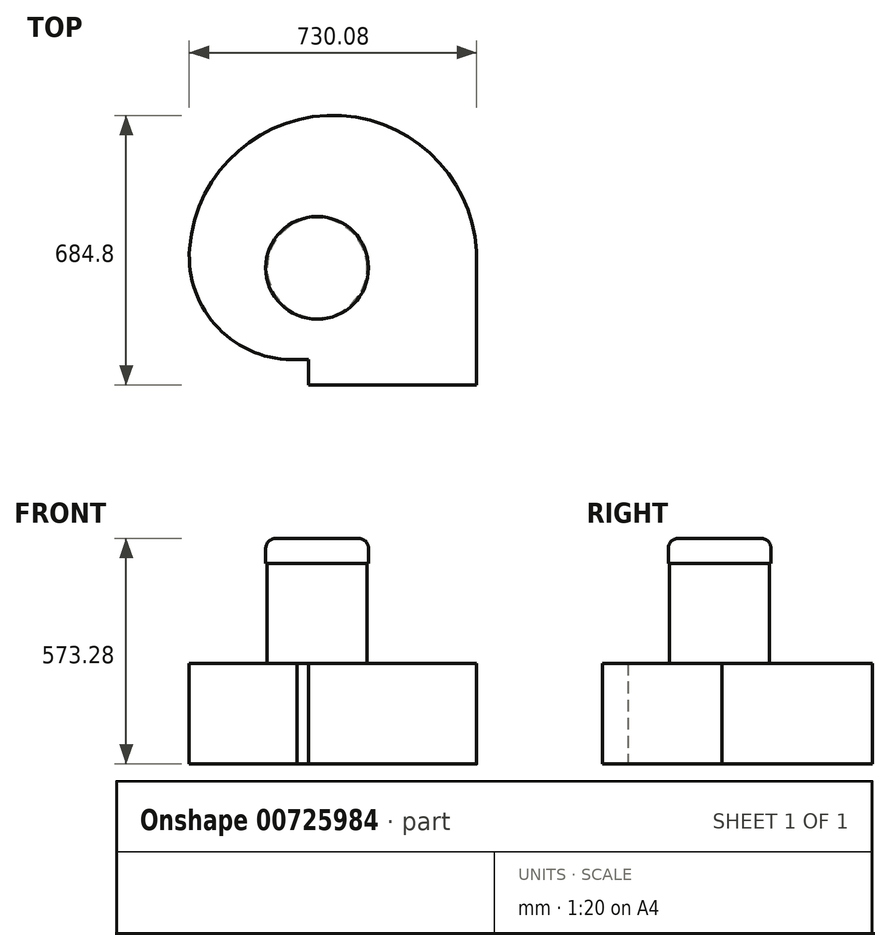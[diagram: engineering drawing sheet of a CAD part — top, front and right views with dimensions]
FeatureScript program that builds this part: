
annotation { "Feature Type Name" : "Feature", "Feature Type Description" : "" }
export const myFeature = defineFeature(function(context is Context, id is Id, definition is map)
    precondition{}
    {
        {
            var Q0;
            Q0=qCreatedBy(makeId("Top.planeOp"),FACE);
            var sketch = newSketch(context, id + "F0", { "sketchPlane" : qUnion([Q0])});
            skLineSegment(sketch, "E0.bottom", {"start": v(0, 0) * mm, "end": v(60.56, 0) * mm, "construction": true});
            skLineSegment(sketch, "E0.top", {"start": v(0, 43.5) * mm, "end": v(60.56, 43.5) * mm, "construction": true});
            skLineSegment(sketch, "E0.left", {"start": v(0, 0) * mm, "end": v(0, 43.5) * mm, "construction": true});
            skLineSegment(sketch, "E0.right", {"start": v(60.56, 0) * mm, "end": v(60.56, 43.5) * mm, "construction": true});
            skLineSegment(sketch, "E1", {"start": v(60.56, 43.5) * mm, "end": v(333.53, 43.5) * mm, "construction": true});
            skLineSegment(sketch, "E2", {"start": v(0, 43.5) * mm, "end": v(0, 380.21) * mm, "construction": true});
            skLineSegment(sketch, "E3", {"start": v(0, 0) * mm, "end": v(-395.45, 0) * mm, "construction": true});
            skLineSegment(sketch, "E4", {"start": v(60.56, 0) * mm, "end": v(60.56, -239.05) * mm, "construction": true});
            skArc(sketch, "E5.MirrorCS", {"start": v(-333.53, 43.5) * mm, "mid": v(52.4, 380.85) * mm, "end": v(395.45, 0) * mm});
            skLineSegment(sketch, "E6.MirrorCS", {"start": v(395.45, 0) * mm, "end": v(395.45, -303.3) * mm});
            skLineSegment(sketch, "E7.MirrorCS", {"start": v(395.45, -303.3) * mm, "end": v(-31.52, -303.3) * mm});
            skLineSegment(sketch, "E8.MirrorCS", {"start": v(-31.52, -239.05) * mm, "end": v(-31.52, -303.3) * mm});
            skLineSegment(sketch, "E9.MirrorCS", {"start": v(-60.56, -239.05) * mm, "end": v(-31.52, -239.05) * mm});
            skArc(sketch, "E10.MirrorCS", {"start": v(-333.53, 43.5) * mm, "mid": v(-260.36, -158.94) * mm, "end": v(-60.56, -239.05) * mm});
            skSolve(sketch);
        }
        {
            var Q0;
            Q0 = qSketchRegion(id + "F0", true);
            extrude(context, id + "F1", {"entities" : qUnion([Q0]), "depth" : 255.52 * mm, "offsetDistance" : 25.4 * mm});
        }
        {
            var Q0;
            Q0=makeQuery(id+"F1.opExtrude","CAP_FACE",FACE,{"disambiguationData":[OSD([sQuery(id+"F0.wireOp",EDGE,"E5.MirrorCS"),sQuery(id+"F0.wireOp",EDGE,"E6.MirrorCS"),sQuery(id+"F0.wireOp",EDGE,"E7.MirrorCS"),sQuery(id+"F0.wireOp",EDGE,"E8.MirrorCS"),sQuery(id+"F0.wireOp",EDGE,"E9.MirrorCS"),sQuery(id+"F0.wireOp",EDGE,"E10.MirrorCS")])],"isStart":false});
            var sketch = newSketch(context, id + "F2", { "sketchPlane" : qUnion([Q0])});
            skLineSegment(sketch, "E11", {"start": v(-31.52, -303.3) * mm, "end": v(-9.42, -303.3) * mm, "construction": true});
            skLineSegment(sketch, "E12", {"start": v(-9.42, -303.3) * mm, "end": v(-9.42, -5.87) * mm, "construction": true});
            skCircle(sketch, "E13", {"center": v(-9.42, -5.87) * mm, "radius": 127 * mm});
            skSolve(sketch);
        }
        {
            var Q0;
            Q0=makeQuery(id+"F2.imprint","IMPRINT",FACE,{"disambiguationData":[TD([[makeQuery(id+"F2.imprint","IMPRINT",EDGE,{"derivedFrom":sQuery(id+"F2.wireOp",EDGE,"E13")}),1.0]])]});
            var Q1;
            Q1=sQuery(id+"F2.wireOp",EDGE,"E13");
            extrude(context, id + "F3", {"entities" : qUnion([Q0]), "operationType" : NewBodyOperationType.ADD, "surfaceEntities" : qUnion([Q1]), "depth" : 254 * mm, "offsetDistance" : 25.4 * mm});
        }
        {
            var Q0;
            Q0=makeQuery(id+"F3.opExtrude","CAP_EDGE",EDGE,{"disambiguationData":[OSD([sQuery(id+"F2.wireOp",EDGE,"E13")])],"isStart":false});
            cPlane(context, id + "F4", {"entities" : qUnion([Q0]), "cplaneType" : CPlaneType.LINE_ANGLE, "offset" : 25.4 * mm, "angle" : 270 * degree, "width" : 152.4 * mm, "height" : 152.4 * mm});
        }
        {
            var Q0;
            Q0=makeQuery(id+"F3.opExtrude","CAP_FACE",FACE,{"disambiguationData":[OSD([sQuery(id+"F2.wireOp",EDGE,"E13")])],"isStart":false});
            var sketch = newSketch(context, id + "F5", { "sketchPlane" : qUnion([Q0])});
            skPoint(sketch, "E14", {"position": v(-9.42, -5.87) * mm});
            skSolve(sketch);
        }
        {
            var Q0;
            Q0=qCreatedBy(id+"F4.planeOp",FACE);
            var sketch = newSketch(context, id + "F6", { "sketchPlane" : qUnion([Q0])});
            skPoint(sketch, "E15.visualSharp", {"position": v(145.3, 575.02) * mm});
            skArc(sketch, "E15.filletArc", {"start": v(121.13, 547.88) * mm, "mid": v(113.7, 565.84) * mm, "end": v(95.73, 573.28) * mm});
            skLineSegment(sketch, "E16", {"start": v(95.73, 573.28) * mm, "end": v(-9.42, 573.28) * mm});
            skLineSegment(sketch, "E17", {"start": v(-9.42, 573.28) * mm, "end": v(-9.42, 509.52) * mm});
            skLineSegment(sketch, "E18", {"start": v(-9.42, 509.52) * mm, "end": v(121.13, 509.52) * mm});
            skLineSegment(sketch, "E19", {"start": v(121.13, 547.88) * mm, "end": v(121.13, 509.52) * mm});
            skSolve(sketch);
        }
        {
            var Q0;
            Q0=makeQuery(id+"F3.opExtrude","CAP_EDGE",EDGE,{"disambiguationData":[OSD([sQuery(id+"F2.wireOp",EDGE,"E13")])],"isStart":false});
            cPlane(context, id + "F7", {"entities" : qUnion([Q0]), "cplaneType" : CPlaneType.LINE_ANGLE, "offset" : 25.4 * mm, "angle" : 0 * degree, "width" : 152.4 * mm, "height" : 152.4 * mm});
        }
        {
            var Q0;
            Q0=qCreatedBy(id+"F7.planeOp",FACE);
            var sketch = newSketch(context, id + "F8", { "sketchPlane" : qUnion([Q0])});
            skLineSegment(sketch, "E20", {"start": v(-5.87, 509.52) * mm, "end": v(-5.87, 540.9) * mm});
            skSolve(sketch);
        }
        {
            var Q0;
            Q0 = qSketchRegion(id + "F6", true);
            var Q1;
            Q1=sQuery(id+"F8.wireOp",EDGE,"E20");
            revolve(context, id + "F9", {"operationType" : NewBodyOperationType.ADD, "surfaceOperationType" : NewSurfaceOperationType.NEW, "entities" : qUnion([Q0]), "axis" : qUnion([Q1]), "revolveType" : RevolveType.FULL});
        }
    });
